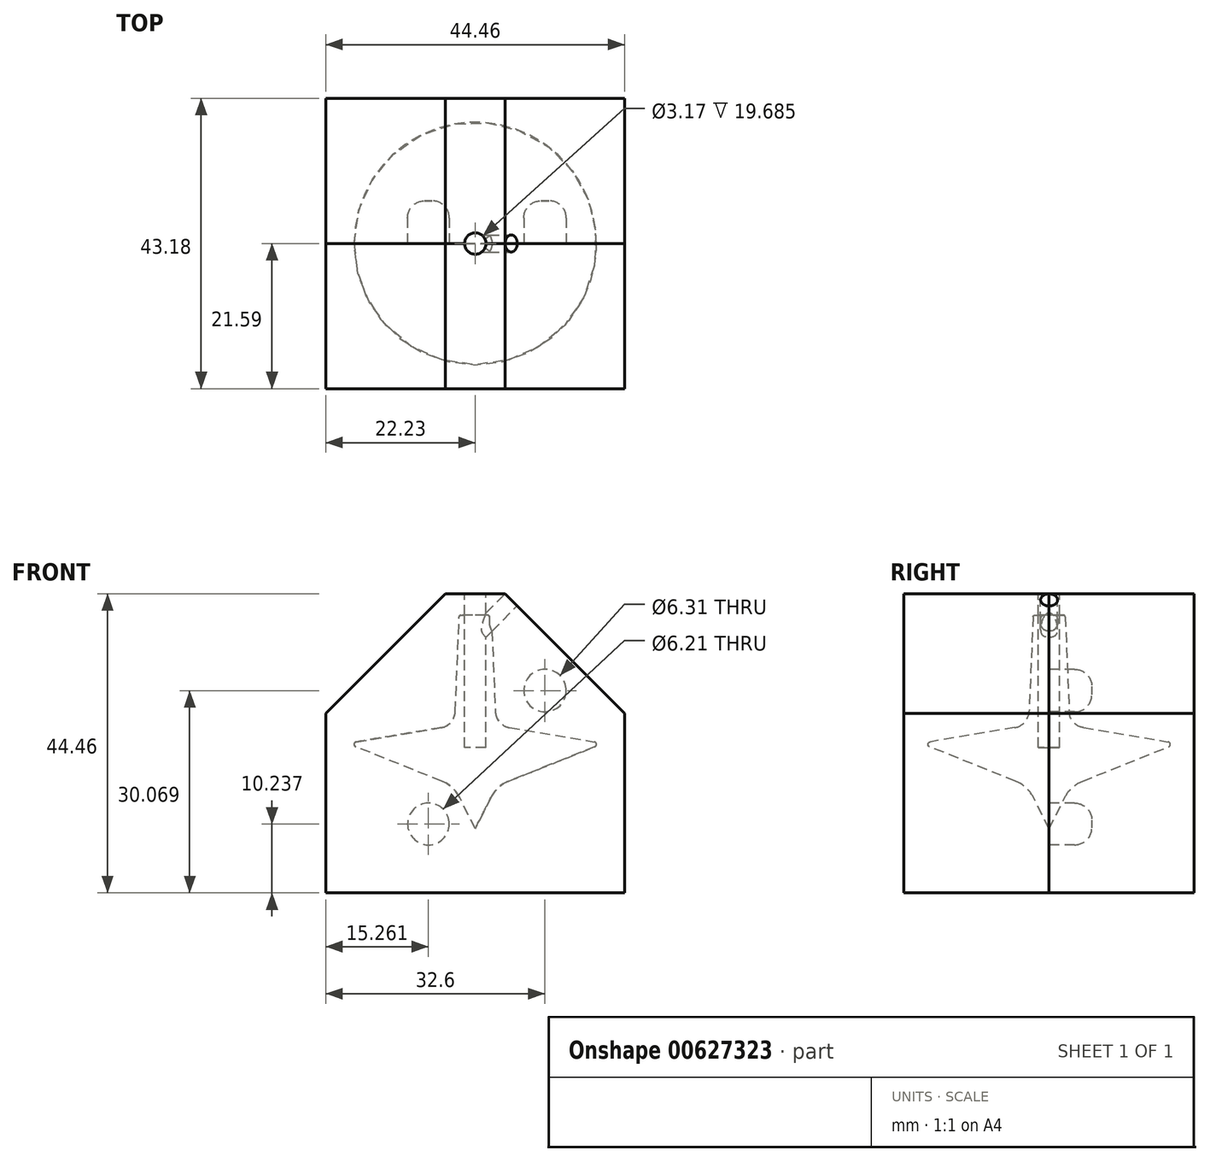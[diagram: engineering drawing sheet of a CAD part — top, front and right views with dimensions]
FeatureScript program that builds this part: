
annotation { "Feature Type Name" : "Feature", "Feature Type Description" : "" }
export const myFeature = defineFeature(function(context is Context, id is Id, definition is map)
    precondition{}
    {
        {
            var Q0;
            Q0=qCreatedBy(makeId("Front.planeOp"),FACE);
            var sketch = newSketch(context, id + "F0", { "sketchPlane" : qUnion([Q0])});
            skLineSegment(sketch, "E0", {"start": v(0, 0) * mm, "end": v(0, 19.05) * mm});
            skLineSegment(sketch, "E1", {"start": v(0, 19.05) * mm, "end": v(2.38, 19.05) * mm});
            skLineSegment(sketch, "E2", {"start": v(3.06, 2.66) * mm, "end": v(19.05, 0) * mm});
            skLineSegment(sketch, "E3", {"start": v(3.06, 2.66) * mm, "end": v(2.38, 19.05) * mm});
            skLineSegment(sketch, "E4", {"start": v(0, 19.05) * mm, "end": v(0, 0) * mm});
            skLineSegment(sketch, "E5", {"start": v(3.18, -6.35) * mm, "end": v(19.05, 0) * mm});
            skLineSegment(sketch, "E6", {"start": v(0, -6.35) * mm, "end": v(0, 0) * mm});
            skLineSegment(sketch, "E7", {"start": v(0, -6.35) * mm, "end": v(0, -12.7) * mm});
            skLineSegment(sketch, "E8", {"start": v(0, -12.7) * mm, "end": v(3.18, -6.35) * mm});
            skLineSegment(sketch, "E9", {"start": v(0, 19.05) * mm, "end": v(0, -12.7) * mm});
            skSolve(sketch);
        }
        {
            var Q0;
            Q0 = qSketchRegion(id + "F0", true);
            var Q1;
            Q1=sQuery(id+"F0.wireOp",EDGE,"E9");
            revolve(context, id + "F1", {"entities" : qUnion([Q0]), "axis" : qUnion([Q1]), "revolveType" : RevolveType.FULL});
        }
        {
            var Q0;
            Q0=makeQuery(id+"F1.opRevolve","SWEPT_EDGE",EDGE,{"disambiguationData":[OSD([sQuery(id+"F0.wireOp",EDGE,"E2"),sQuery(id+"F0.wireOp",EDGE,"E5")])]});
            fillet(context, id + "F2", {"entities" : qUnion([Q0]), "radius" : 0.38 * mm, "tangentPropagation" : true, "allowEdgeOverflow" : false});
        }
        {
            var Q0;
            Q0=makeQuery(id+"F1.opRevolve","SWEPT_EDGE",EDGE,{"disambiguationData":[OSD([sQuery(id+"F0.wireOp",EDGE,"E5"),sQuery(id+"F0.wireOp",EDGE,"E8")])]});
            fillet(context, id + "F3", {"entities" : qUnion([Q0]), "radius" : 5.08 * mm, "tangentPropagation" : true, "allowEdgeOverflow" : false});
        }
        {
            var Q0;
            Q0=makeQuery(id+"F1.opRevolve","SWEPT_EDGE",EDGE,{"disambiguationData":[OSD([sQuery(id+"F0.wireOp",EDGE,"E1"),sQuery(id+"F0.wireOp",EDGE,"E3")])]});
            fillet(context, id + "F4", {"entities" : qUnion([Q0]), "radius" : 0.25 * mm, "tangentPropagation" : true, "allowEdgeOverflow" : false});
        }
        {
            var Q0;
            Q0=makeQuery(id+"F1.opRevolve","SWEPT_EDGE",EDGE,{"disambiguationData":[OSD([sQuery(id+"F0.wireOp",EDGE,"E2"),sQuery(id+"F0.wireOp",EDGE,"E3")])]});
            fillet(context, id + "F5", {"entities" : qUnion([Q0]), "radius" : 2.54 * mm, "tangentPropagation" : true, "allowEdgeOverflow" : false});
        }
        {
            var Q0;
            Q0=qCreatedBy(makeId("Front.planeOp"),FACE);
            var sketch = newSketch(context, id + "F6", { "sketchPlane" : qUnion([Q0])});
            skLineSegment(sketch, "E10.bottom", {"start": v(-22.22, 22.23) * mm, "end": v(22.23, 22.23) * mm});
            skLineSegment(sketch, "E10.top", {"start": v(-22.23, -22.23) * mm, "end": v(22.22, -22.23) * mm});
            skLineSegment(sketch, "E10.left", {"start": v(-22.22, 22.23) * mm, "end": v(-22.23, -22.22) * mm});
            skLineSegment(sketch, "E10.right", {"start": v(22.23, 22.23) * mm, "end": v(22.22, -22.22) * mm});
            skPoint(sketch, "E10.middle", {"position": v(0, 0) * mm});
            skPoint(sketch, "E11.end.orphan", {"position": v(0, 22.23) * mm});
            skSolve(sketch);
        }
        {
            var Q0;
            Q0 = qSketchRegion(id + "F6", true);
            extrude(context, id + "F7", {"entities" : qUnion([Q0]), "depth" : 21.59 * mm, "offsetDistance" : 25.4 * mm});
        }
        {
            var Q0;
            Q0=makeQuery(id+"F1.opRevolve","SWEPT_BODY",BODY,{"disambiguationData":[OSD([sQuery(id+"F0.wireOp",EDGE,"E1"),sQuery(id+"F0.wireOp",EDGE,"E2"),sQuery(id+"F0.wireOp",EDGE,"E3"),sQuery(id+"F0.wireOp",EDGE,"E5"),sQuery(id+"F0.wireOp",EDGE,"E8"),sQuery(id+"F0.wireOp",EDGE,"E9")])]});
            var Q1;
            Q1=makeQuery(id+"F7.opExtrude","SWEPT_BODY",BODY,{"disambiguationData":[OSD([sQuery(id+"F6.wireOp",EDGE,"E10.bottom"),sQuery(id+"F6.wireOp",EDGE,"E10.top"),sQuery(id+"F6.wireOp",EDGE,"E10.left"),sQuery(id+"F6.wireOp",EDGE,"E10.right")])]});
            booleanBodies(context, id + "F8", {"operationType" : BooleanOperationType.SUBTRACTION, "tools" : qUnion([Q0]), "targets" : qUnion([Q1]), "keepTools" : true});
        }
        {
            var Q0;
            Q0=makeQuery(id+"F7.opExtrude","CAP_FACE",FACE,{"disambiguationData":[OSD([sQuery(id+"F6.wireOp",EDGE,"E10.bottom"),sQuery(id+"F6.wireOp",EDGE,"E10.top"),sQuery(id+"F6.wireOp",EDGE,"E10.left"),sQuery(id+"F6.wireOp",EDGE,"E10.right")])],"isStart":true});
            var sketch = newSketch(context, id + "F9", { "sketchPlane" : qUnion([Q0])});
            skCircle(sketch, "E12", {"center": v(-10.37, 7.84) * mm, "radius": 3.16 * mm});
            skCircle(sketch, "E13", {"center": v(6.97, -12) * mm, "radius": 3.1 * mm});
            skLineSegment(sketch, "E14.bottom", {"start": v(22.23, -22.22) * mm, "end": v(-22.23, -22.23) * mm});
            skLineSegment(sketch, "E14.top", {"start": v(22.23, 22.23) * mm, "end": v(-22.23, 22.22) * mm});
            skLineSegment(sketch, "E14.left", {"start": v(22.23, -22.22) * mm, "end": v(22.23, 22.23) * mm});
            skLineSegment(sketch, "E14.right", {"start": v(-22.23, -22.23) * mm, "end": v(-22.23, 22.22) * mm});
            skPoint(sketch, "E14.middle", {"position": v(0, 0) * mm});
            skSolve(sketch);
        }
        {
            var Q0;
            Q0=makeQuery(id+"F9.imprint","IMPRINT",FACE,{"disambiguationData":[TD([[makeQuery(id+"F9.imprint","IMPRINT",EDGE,{"derivedFrom":sQuery(id+"F9.wireOp",EDGE,"E13")}),1.0]])]});
            var Q1;
            Q1=makeQuery(id+"F9.imprint","IMPRINT",FACE,{"disambiguationData":[TD([[makeQuery(id+"F9.imprint","IMPRINT",EDGE,{"derivedFrom":sQuery(id+"F9.wireOp",EDGE,"E12")}),1.0]])]});
            extrude(context, id + "F10", {"entities" : qUnion([Q0, Q1]), "operationType" : NewBodyOperationType.ADD, "depth" : 6.35 * mm, "offsetDistance" : 25.4 * mm});
        }
        {
            var Q0;
            Q0=makeQuery(id+"F10.opExtrude","CAP_FACE",FACE,{"disambiguationData":[OSD([sQuery(id+"F9.wireOp",EDGE,"E12")])],"isStart":false});
            var Q1;
            Q1=makeQuery(id+"F10.opExtrude","CAP_FACE",FACE,{"disambiguationData":[OSD([sQuery(id+"F9.wireOp",EDGE,"E13")])],"isStart":false});
            fillet(context, id + "F11", {"entities" : qUnion([Q0, Q1]), "radius" : 2.54 * mm, "tangentPropagation" : true, "allowEdgeOverflow" : false});
        }
        {
            var Q0;
            Q0=makeQuery(id+"F9.imprint","IMPRINT",FACE,{"disambiguationData":[TD([[makeQuery(id+"F9.imprint","IMPRINT",EDGE,{"derivedFrom":sQuery(id+"F9.wireOp",EDGE,"E12")}),-1.0]])]});
            var Q1;
            {var subQ0=makeQuery(id+"F7.opExtrude","CAP_FACE",FACE,{"disambiguationData":[OSD([sQuery(id+"F6.wireOp",EDGE,"E10.bottom"),sQuery(id+"F6.wireOp",EDGE,"E10.top"),sQuery(id+"F6.wireOp",EDGE,"E10.left"),sQuery(id+"F6.wireOp",EDGE,"E10.right")])],"isStart":true});var subQ2=sQuery(id+"F0.wireOp",EDGE,"E1");Q1=makeQuery(id+"F9.imprint","IMPRINT",FACE,{"disambiguationData":[TD([[makeQuery(id+"F9.imprint","IMPRINT",EDGE,{"derivedFrom":makeQuery(id+"F8.opBoolean","INTERSECT",EDGE,{"derivedFrom":[makeQuery(id+"F1.opRevolve","SWEPT_FACE",FACE,{"disambiguationData":[OSD([subQ2])]}),subQ0]})}),-1.0]])]});}
            var Q2;
            Q2=makeQuery(id+"F9.imprint","IMPRINT",FACE,{"disambiguationData":[TD([[makeQuery(id+"F9.imprint","IMPRINT",EDGE,{"derivedFrom":sQuery(id+"F9.wireOp",EDGE,"E13")}),1.0]])]});
            var Q3;
            Q3=makeQuery(id+"F9.imprint","IMPRINT",FACE,{"disambiguationData":[TD([[makeQuery(id+"F9.imprint","IMPRINT",EDGE,{"derivedFrom":sQuery(id+"F9.wireOp",EDGE,"E12")}),1.0]])]});
            extrude(context, id + "F12", {"entities" : qUnion([Q0, Q1, Q2, Q3]), "depth" : 21.59 * mm, "offsetDistance" : 25.4 * mm});
        }
        {
            var Q0;
            Q0=makeQuery(id+"F1.opRevolve","SWEPT_BODY",BODY,{"disambiguationData":[OSD([sQuery(id+"F0.wireOp",EDGE,"E1"),sQuery(id+"F0.wireOp",EDGE,"E2"),sQuery(id+"F0.wireOp",EDGE,"E3"),sQuery(id+"F0.wireOp",EDGE,"E5"),sQuery(id+"F0.wireOp",EDGE,"E8"),sQuery(id+"F0.wireOp",EDGE,"E9")])]});
            var Q1;
            Q1=makeQuery(id+"F12.opExtrude","SWEPT_BODY",BODY,{"disambiguationData":[OSD([sQuery(id+"F6.wireOp",EDGE,"E10.bottom"),sQuery(id+"F6.wireOp",EDGE,"E10.top"),sQuery(id+"F6.wireOp",EDGE,"E10.left"),sQuery(id+"F6.wireOp",EDGE,"E10.right"),sQuery(id+"F9.wireOp",EDGE,"E14.bottom"),sQuery(id+"F9.wireOp",EDGE,"E14.top"),sQuery(id+"F9.wireOp",EDGE,"E14.left"),sQuery(id+"F9.wireOp",EDGE,"E14.right")])]});
            var Q2;
            Q2=makeQuery(id+"F10.opExtrude","SWEPT_BODY",BODY,{"disambiguationData":[OSD([sQuery(id+"F9.wireOp",EDGE,"E12")])]});
            var Q3;
            Q3=makeQuery(id+"F10.opExtrude","SWEPT_BODY",BODY,{"disambiguationData":[OSD([sQuery(id+"F9.wireOp",EDGE,"E13")])]});
            booleanBodies(context, id + "F13", {"operationType" : BooleanOperationType.SUBTRACTION, "tools" : qUnion([Q0]), "targets" : qUnion([Q1, Q2, Q3]), "keepTools" : true});
        }
        {
            var Q0;
            Q0=makeQuery(id+"F9.imprint","IMPRINT",FACE,{"disambiguationData":[TD([[makeQuery(id+"F9.imprint","IMPRINT",EDGE,{"derivedFrom":sQuery(id+"F9.wireOp",EDGE,"E13")}),1.0]])]});
            var Q1;
            Q1=makeQuery(id+"F9.imprint","IMPRINT",FACE,{"disambiguationData":[TD([[makeQuery(id+"F9.imprint","IMPRINT",EDGE,{"derivedFrom":sQuery(id+"F9.wireOp",EDGE,"E12")}),1.0]])]});
            extrude(context, id + "F14", {"entities" : qUnion([Q0, Q1]), "operationType" : NewBodyOperationType.REMOVE, "depth" : 6.35 * mm, "offsetDistance" : 25.4 * mm});
        }
        {
            var Q0;
            Q0=makeQuery(id+"F14.boolean.opBoolean","COPY",EDGE,{"derivedFrom":makeQuery(id+"F14.opExtrude","CAP_EDGE",EDGE,{"disambiguationData":[OSD([sQuery(id+"F9.wireOp",EDGE,"E12")])],"isStart":false})});
            var Q1;
            Q1=makeQuery(id+"F14.boolean.opBoolean","COPY",FACE,{"derivedFrom":makeQuery(id+"F14.opExtrude","CAP_FACE",FACE,{"disambiguationData":[OSD([sQuery(id+"F9.wireOp",EDGE,"E13")])],"isStart":false})});
            fillet(context, id + "F15", {"entities" : qUnion([Q0, Q1]), "radius" : 2.54 * mm, "tangentPropagation" : true, "allowEdgeOverflow" : false});
        }
        {
            var Q0;
            Q0=makeQuery(id+"F12.opExtrude","SWEPT_EDGE",EDGE,{"disambiguationData":[OSD([sQuery(id+"F9.wireOp",EDGE,"E14.top"),sQuery(id+"F9.wireOp",EDGE,"E14.left")])]});
            var Q1;
            Q1=makeQuery(id+"F12.opExtrude","SWEPT_EDGE",EDGE,{"disambiguationData":[OSD([sQuery(id+"F9.wireOp",EDGE,"E14.top"),sQuery(id+"F9.wireOp",EDGE,"E14.right")])]});
            chamfer(context, id + "F16", {"entities" : qUnion([Q0, Q1]), "width" : 17.78 * mm, "tangentPropagation" : true});
        }
        {
            var Q0;
            Q0=makeQuery(id+"F7.opExtrude","SWEPT_EDGE",EDGE,{"disambiguationData":[OSD([sQuery(id+"F6.wireOp",EDGE,"E10.bottom"),sQuery(id+"F6.wireOp",EDGE,"E10.right")])]});
            var Q1;
            Q1=makeQuery(id+"F7.opExtrude","SWEPT_EDGE",EDGE,{"disambiguationData":[OSD([sQuery(id+"F6.wireOp",EDGE,"E10.bottom"),sQuery(id+"F6.wireOp",EDGE,"E10.left")])]});
            chamfer(context, id + "F17", {"entities" : qUnion([Q0, Q1]), "width" : 17.78 * mm, "tangentPropagation" : true});
        }
        {
            var Q0;
            Q0=makeQuery(id+"F7.opExtrude","SWEPT_FACE",FACE,{"disambiguationData":[OSD([sQuery(id+"F6.wireOp",EDGE,"E10.bottom")])]});
            var sketch = newSketch(context, id + "F18", { "sketchPlane" : qUnion([Q0])});
            skCircle(sketch, "E15", {"center": v(0, 0) * mm, "radius": 1.59 * mm});
            skSolve(sketch);
        }
        {
            var Q0;
            {var subQ0=sQuery(id+"F18.wireOp",EDGE,"E15");var subQ1=makeQuery(id+"F7.opExtrude","CAP_EDGE",EDGE,{"disambiguationData":[OSD([sQuery(id+"F6.wireOp",EDGE,"E10.bottom")])],"isStart":true});var subQ2=makeQuery(id+"F18.imprint","INTERSECT",VERTEX,{"disambiguationData":[OD(0.0)],"derivedFrom":[subQ1,subQ0]});Q0=makeQuery(id+"F18.imprint","IMPRINT",FACE,{"disambiguationData":[TD([[makeQuery(id+"F18.imprint","IMPRINT",EDGE,{"disambiguationData":[TD([[subQ2,-1.0]])],"derivedFrom":subQ0}),1.0]])]});}
            var Q1;
            Q1=makeQuery(id+"F18.imprint","IMPRINT",FACE,{"disambiguationData":[TD([[makeQuery(id+"F18.imprint","IMPRINT",EDGE,{"derivedFrom":sQuery(id+"F18.wireOp",EDGE,"vqyCJoYO-8QYk-CJn7-dKBR-rKrTtC1H0AlV")}),1.0]])]});
            var Q2;
            {var subQ0=sQuery(id+"F18.wireOp",EDGE,"E15");var subQ1=makeQuery(id+"F7.opExtrude","CAP_EDGE",EDGE,{"disambiguationData":[OSD([sQuery(id+"F6.wireOp",EDGE,"E10.bottom")])],"isStart":true});var subQ2=makeQuery(id+"F18.imprint","INTERSECT",VERTEX,{"disambiguationData":[OD(0.0)],"derivedFrom":[subQ1,subQ0]});Q2=makeQuery(id+"F18.imprint","IMPRINT",FACE,{"disambiguationData":[TD([[makeQuery(id+"F18.imprint","IMPRINT",EDGE,{"disambiguationData":[TD([[subQ2,1.0]])],"derivedFrom":subQ0}),1.0]])]});}
            extrude(context, id + "F19", {"entities" : qUnion([Q0, Q1, Q2]), "operationType" : NewBodyOperationType.REMOVE, "oppositeDirection" : true, "depth" : 22.86 * mm, "offsetDistance" : 25.4 * mm});
        }
        {
            var Q0;
            {var subQ0=sQuery(id+"F18.wireOp",EDGE,"E15");var subQ1=makeQuery(id+"F7.opExtrude","CAP_EDGE",EDGE,{"disambiguationData":[OSD([sQuery(id+"F6.wireOp",EDGE,"E10.bottom")])],"isStart":true});var subQ2=makeQuery(id+"F18.imprint","INTERSECT",VERTEX,{"disambiguationData":[OD(0.0)],"derivedFrom":[subQ1,subQ0]});Q0=makeQuery(id+"F18.imprint","IMPRINT",FACE,{"disambiguationData":[TD([[makeQuery(id+"F18.imprint","IMPRINT",EDGE,{"disambiguationData":[TD([[subQ2,1.0]])],"derivedFrom":subQ0}),1.0]])]});}
            var Q1;
            Q1=makeQuery(id+"F18.imprint","IMPRINT",FACE,{"disambiguationData":[TD([[makeQuery(id+"F18.imprint","IMPRINT",EDGE,{"derivedFrom":sQuery(id+"F18.wireOp",EDGE,"vqyCJoYO-8QYk-CJn7-dKBR-rKrTtC1H0AlV")}),1.0]])]});
            extrude(context, id + "F20", {"entities" : qUnion([Q0, Q1]), "operationType" : NewBodyOperationType.REMOVE, "oppositeDirection" : true, "depth" : 22.86 * mm, "offsetDistance" : 25.4 * mm});
        }
        {
            var Q0;
            Q0=makeQuery(id+"F16.opChamfer","BLEND_FACE",FACE,{"disambiguationData":[OSD([sQuery(id+"F9.wireOp",EDGE,"E14.top"),sQuery(id+"F9.wireOp",EDGE,"E14.right")])]});
            var sketch = newSketch(context, id + "F21", { "sketchPlane" : qUnion([Q0])});
            skLineSegment(sketch, "E16", {"start": v(0, 12.57) * mm, "end": v(0, 11.3) * mm});
            skCircle(sketch, "E17", {"center": v(0, 11.3) * mm, "radius": 0.64 * mm});
            skSolve(sketch);
        }
        {
            var Q0;
            Q0 = qSketchRegion(id + "F21", true);
            extrude(context, id + "F22", {"entities" : qUnion([Q0]), "operationType" : NewBodyOperationType.REMOVE, "oppositeDirection" : true, "depth" : 7.62 * mm, "offsetDistance" : 25.4 * mm});
        }
        {
            var Q0;
            Q0=makeQuery(id+"F17.opChamfer","BLEND_FACE",FACE,{"disambiguationData":[OSD([sQuery(id+"F6.wireOp",EDGE,"E10.bottom"),sQuery(id+"F6.wireOp",EDGE,"E10.right")])]});
            var sketch = newSketch(context, id + "F23", { "sketchPlane" : qUnion([Q0])});
            skLineSegment(sketch, "E18", {"start": v(0, 12.57) * mm, "end": v(0, 11.3) * mm});
            skCircle(sketch, "E19", {"center": v(0, 11.3) * mm, "radius": 1.27 * mm});
            skSolve(sketch);
        }
        {
            var Q0;
            {var subQ0=sQuery(id+"F23.wireOp",EDGE,"E18");Q0=makeQuery(id+"F23.imprint","IMPRINT",FACE,{"disambiguationData":[TD([[makeQuery(id+"F23.imprint","IMPRINT",EDGE,{"derivedFrom":subQ0}),-1.0]])]});}
            var Q1;
            {var subQ0=sQuery(id+"F23.wireOp",EDGE,"E18");Q1=makeQuery(id+"F23.imprint","IMPRINT",FACE,{"disambiguationData":[TD([[makeQuery(id+"F23.imprint","IMPRINT",EDGE,{"derivedFrom":subQ0}),1.0]])]});}
            extrude(context, id + "F24", {"entities" : qUnion([Q0, Q1]), "operationType" : NewBodyOperationType.REMOVE, "oppositeDirection" : true, "depth" : 7.62 * mm, "offsetDistance" : 25.4 * mm});
        }
        {
            var Q0;
            {var subQ0=sQuery(id+"F23.wireOp",EDGE,"E18");Q0=makeQuery(id+"F23.imprint","IMPRINT",FACE,{"disambiguationData":[TD([[makeQuery(id+"F23.imprint","IMPRINT",EDGE,{"derivedFrom":subQ0}),1.0]])]});}
            extrude(context, id + "F25", {"entities" : qUnion([Q0]), "operationType" : NewBodyOperationType.REMOVE, "oppositeDirection" : true, "depth" : 7.62 * mm, "offsetDistance" : 25.4 * mm});
        }
    });
